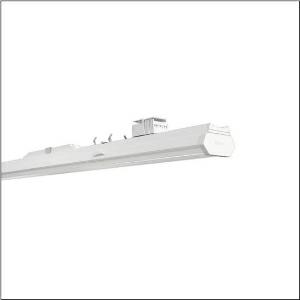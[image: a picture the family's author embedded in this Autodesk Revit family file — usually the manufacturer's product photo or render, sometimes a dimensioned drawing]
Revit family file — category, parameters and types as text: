
# Revit family: licross_r__11_protected_mo_51td11cn49xg_045e
name_source: partatom
category: Lighting Fixtures
units: mm (PartAtom-declared; Revit-internal decimal feet)

## family parameters
Cut with Voids When Loaded = No
Host = Face
Light Source = No
Part Type = Normal
Room Calculation Point = No
Round Connector Dimension = Use Diameter
Shared = No

## types (1)
- --- (1 x LED, 9030 lm, 49.4 W, 4000K)
    Apparent Load = 49 VA
    CIE Flux Codes = 83 94 98 100 100
    Color Rendering = 80
    Color Temperature = 4000K
    Default Elevation = 1800 mm
    Description = Licross® 11 Protected MO, luminaire insert, of sheet steel, galvanised, coil coated, white, length: 1.500mm, width: 90mm, height: 101mm, LED rated luminous flux: 9.030lm, light colour: 840, control gear: ON/OFF Multilumen, CLOi, with plug, 3-pole, with phase selection, mains connection: 220..240V, AC, 50/60Hz, start of lifetime: 49W, end of service life: 55W, halogen-free wiring, primary light control with lens, of plastic, primary optical cover: cover, of PMMA, light emission: direct distribution, primary light characteristic: symmetric, protection rating (complete): IP54, insulation class (complete): insulation class I (protective earthing), certification: CE, ENEC, VDE, UKCA, protection symbol: D if used in an environment with non-conductive dust loads with corresponding accessories, impact resistance: IK06, permissible ambient temperature for indoor applications: -35..+40°C, corresponds to IFS (International Featured Standards) requirements for safety and quality in the food industry, reducing of maximum allowable ambient temperature of 5°C with ceiling mounting, LABS conformity tested according to VDMA 24364:2018-05, packaging unit: 1 piece
    Height = 92 mm
    Lamp = 1 x LED
    Lamp Light Flux = 9030 lm
    Lamp Power = 49.4 W
    Lamp count = 1
    Length = 1500 mm
    Luminous efficacy = 183 lm/W
    Manufacturer = Siteco
    ModVariant = No
    Model = 51TD11CN49XG
    Mounting Place = Ceiling
    Mounting Type = Pendant
    Number of Poles = 1
    OnlyDefault = Yes
    Power Factor = 1
    Product Name = Licross® 11 Protected MO
    Product group = luminaire insert
    ProductGroupID = 902
    Protection Class = Protection class I
    Protection Degree = IP 54
    RLX_Detail_Level = 1
    RLX_Emergency_Light_Flux = 0 lm
    RLX_Emergency_Type = 0
    RLX_Emergency_Type_DB = No
    RlxData = <blob elided: 21825 chars, md5=e7cd32d7>
    Socket = socket
    Standby Power = 0 W
    System Light Flux = 9030 lm
    System Power = 49 W
    Type Comments = factory setting: luminous flux: 100 % | (A | C | E) | 113 mA
    Type Image = l_1256145.jpg
    URL = http://relux.com
    VarID = @adj_085756
    Voltage = 0 V
    Weight = 0.00 kg
    Width = 88 mm

## geometry (parser evidence)
native form markers: Blend x4, Sweep x12
no freeform markers — native parametric forms only
